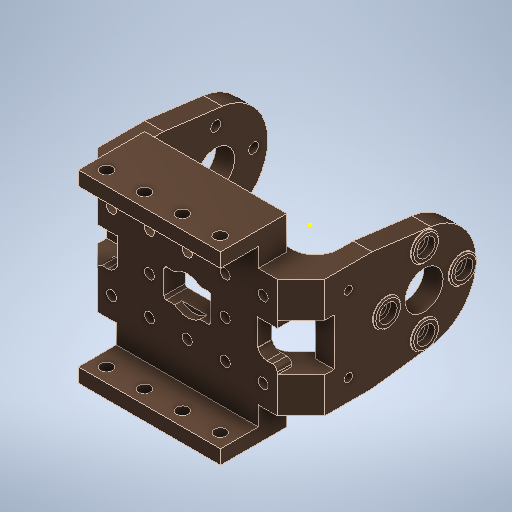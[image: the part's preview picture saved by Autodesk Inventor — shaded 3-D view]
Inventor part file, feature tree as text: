
AUTODESK INVENTOR PART (.ipt)
format: ipt  version: 2025 (Build 290162000, 162)  size: 1,553,920 bytes
history: native  units: in
note: dims shown in document units (in); Inventor stores cm internally (conversion verified against a paired STEP export)
features: sketch x12, extrude x11, other x2, direct_edit x1, plane x1, imported_body x1
ambient origin geometry x8: Origin, YZ Plane, XZ Plane, XY Plane, X Axis, Y Axis, Z Axis, Center Point
bodies: Solid1 (feature_tree)
feature tree (28):
  direct_edit  "Direct Edit1"
  extrude  "Extrusión3"  Depth=0.0394in
  sketch  "Boceto10"  dims[d13=0.2362in d16=0.2756in d17=0.0in]
  plane  "Plano de trabajo2"
  sketch  "Boceto16"  dims[d20=0.2362in d49=0.2362in]
  extrude  "Extrusión15"  Depth=0.2756in TaperAngle=0.0deg
  extrude  "Extrusión16"  Depth=0.2362in
  extrude  "Extrusión17"  Depth=0.2362in
  extrude  "Extrusión18"  Depth=0.2362in
  extrude  "Extrusión19"  Depth=0.1575in
  extrude  "Extrusión20"  Depth=0.2362in
  extrude  "Extrusión21"  [1 undecoded]
  extrude  "Extrusión22"  Depth=0.2756in TaperAngle=0.0deg
  extrude  "Extrusión23"  TaperAngle=0.0deg  [1 undecoded]
  extrude  "Extrusión24"  Depth=0.1181in
  sketch  "Boceto5"  dims[d1=0.0394in d2=0.0394in]
  sketch  "Boceto20"  dims[d50=0.2362in d51=0.2362in]
  sketch  "Boceto21"  dims[d52=0.1575in d56=0.2362in]
  sketch  "Boceto22"  dims[d57=0.2362in d59=0.1575in]
  sketch  "Boceto23"  dims[d60=0.2362in d61=0.2362in]
  sketch  "Boceto24"  dims[d63=0.1575in d66=-0.4921in]
  sketch  "Boceto25"  dims[d80=0.1575in d98=0.2756in d99=0.0in]
  sketch  "Boceto26"  dims[d100=0.2756in d101=0.0in d102=0.0in d103=0.0in]
  sketch  "Boceto27"  dims[d104=0.1181in d105=0.1181in]
  sketch  "Boceto28"  dims[d106=0.1181in d107=0.1181in d108=0.315in d109=0.0in d110=0.0984in d111=0.0984in d113=0.1181in d114=0.9449in d115=0.0in d116=0.0in d117=1.2992in d118=0.2756in d119=0.0in d120=0.315in d121=0.0in d122=0.2756in d123=0.0in d124=0.315in d125=0.0in d126=0.0984in d127=0.315in d128=0.0984in d129=0.315in d130=0.315in d131=0.0in d132=0.0in]
  imported_body  "Base1"
  other  "Size1"
  other  "Size2"
note: 2 required parameter values undecoded (feature->parameter linkage not recoverable at this tier; creation-order binding heuristic only, values carry confidence <= 0.55)
